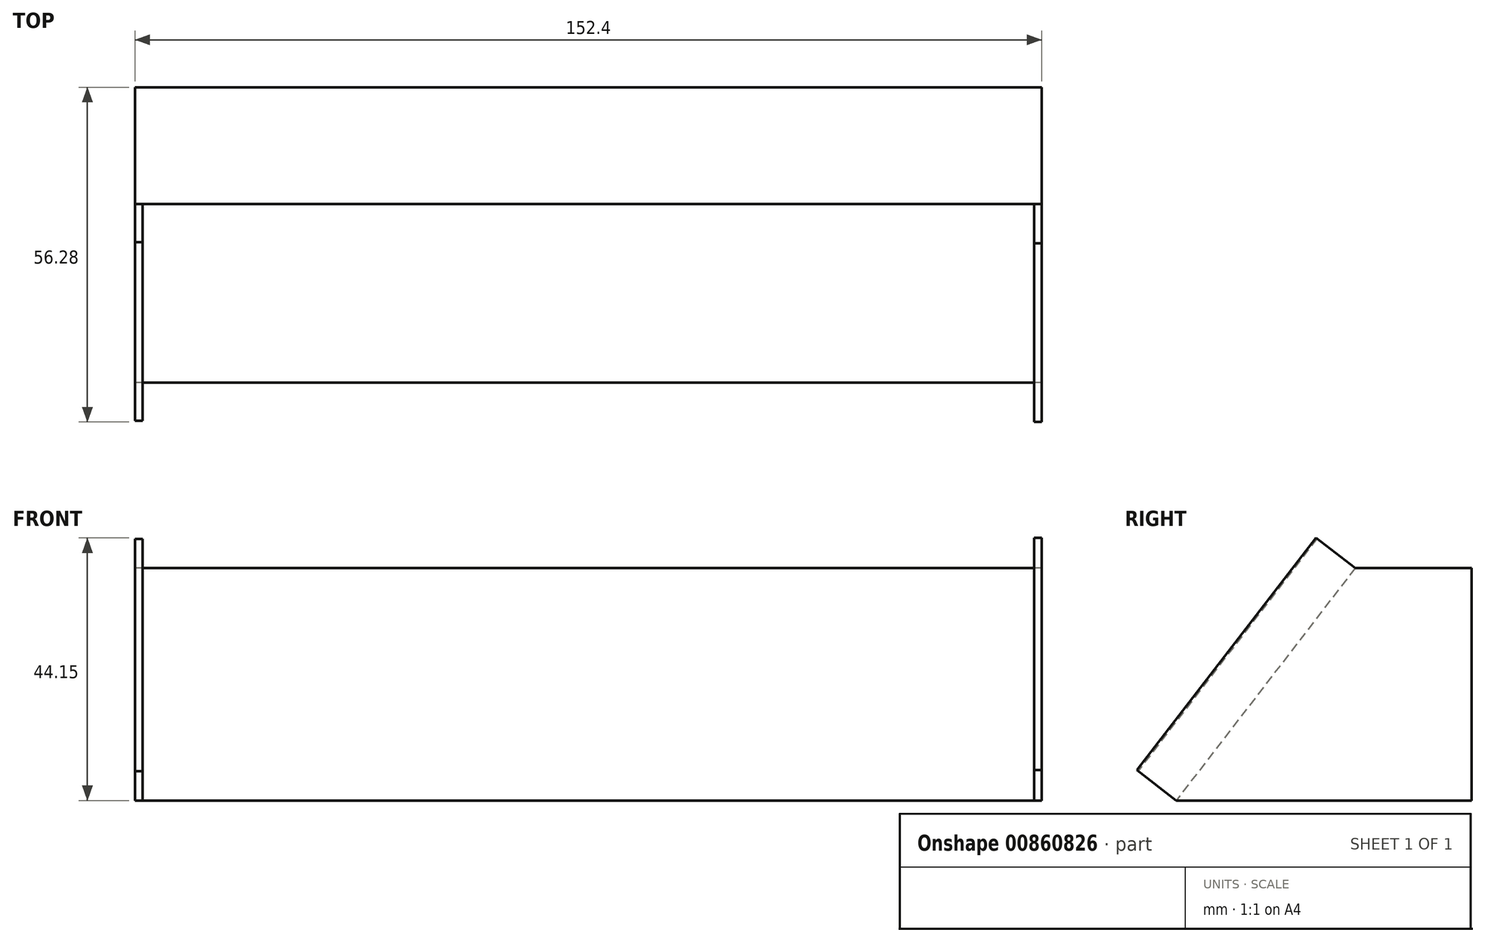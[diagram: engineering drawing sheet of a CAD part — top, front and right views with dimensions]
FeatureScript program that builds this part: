
annotation { "Feature Type Name" : "Feature", "Feature Type Description" : "" }
export const myFeature = defineFeature(function(context is Context, id is Id, definition is map)
    precondition{}
    {
        {
            var Q0;
            Q0=qCreatedBy(makeId("Right.planeOp"),FACE);
            var sketch = newSketch(context, id + "F0", { "sketchPlane" : qUnion([Q0])});
            skLineSegment(sketch, "E0", {"start": v(-3.9, 0) * mm, "end": v(26.18, 0) * mm});
            skLineSegment(sketch, "E1", {"start": v(26.18, 39.07) * mm, "end": v(-3.9, 0) * mm});
            skPoint(sketch, "E2.orphan", {"position": v(-22.96, 0) * mm});
            skLineSegment(sketch, "E3.bottom", {"start": v(26.18, 39.07) * mm, "end": v(45.78, 39.07) * mm});
            skLineSegment(sketch, "E3.top", {"start": v(26.18, 0) * mm, "end": v(45.78, 0) * mm});
            skLineSegment(sketch, "E3.right", {"start": v(45.78, 39.07) * mm, "end": v(45.78, 0) * mm});
            skSolve(sketch);
        }
        {
            var Q0;
            Q0 = qSketchRegion(id + "F0", true);
            extrude(context, id + "F1", {"entities" : qUnion([Q0]), "endBound" : BoundingType.SYMMETRIC, "depth" : 152.4 * mm, "offsetDistance" : 25.4 * mm});
        }
        {
            var Q0;
            Q0=makeQuery(id+"F1.opExtrude","CAP_FACE",FACE,{"disambiguationData":[OSD([sQuery(id+"F0.wireOp",EDGE,"E0"),sQuery(id+"F0.wireOp",EDGE,"E1"),sQuery(id+"F0.wireOp",EDGE,"E3.bottom"),sQuery(id+"F0.wireOp",EDGE,"E3.top"),sQuery(id+"F0.wireOp",EDGE,"E3.right")])],"isStart":false});
            var sketch = newSketch(context, id + "F2", { "sketchPlane" : qUnion([Q0])});
            skLineSegment(sketch, "E4", {"start": v(-3.9, 0) * mm, "end": v(-10.5, 5.09) * mm});
            skLineSegment(sketch, "E5", {"start": v(-10.5, 5.09) * mm, "end": v(19.57, 44.15) * mm});
            skLineSegment(sketch, "E6", {"start": v(19.57, 44.15) * mm, "end": v(26.18, 39.07) * mm});
            skLineSegment(sketch, "E7", {"start": v(26.18, 39.07) * mm, "end": v(-3.9, 0) * mm});
            skSolve(sketch);
        }
        {
            var Q0;
            Q0 = qSketchRegion(id + "F2", true);
            extrude(context, id + "F3", {"entities" : qUnion([Q0]), "operationType" : NewBodyOperationType.ADD, "oppositeDirection" : true, "depth" : 1.27 * mm, "offsetDistance" : 25.4 * mm});
        }
        {
            var Q0;
            Q0=makeQuery(id+"F1.opExtrude","CAP_FACE",FACE,{"disambiguationData":[OSD([sQuery(id+"F0.wireOp",EDGE,"E0"),sQuery(id+"F0.wireOp",EDGE,"E1"),sQuery(id+"F0.wireOp",EDGE,"E3.bottom"),sQuery(id+"F0.wireOp",EDGE,"E3.top"),sQuery(id+"F0.wireOp",EDGE,"E3.right")])],"isStart":true});
            var sketch = newSketch(context, id + "F4", { "sketchPlane" : qUnion([Q0])});
            skLineSegment(sketch, "E8", {"start": v(-26.18, 39.07) * mm, "end": v(-19.75, 44.01) * mm});
            skLineSegment(sketch, "E9", {"start": v(-19.75, 44.01) * mm, "end": v(10.32, 4.95) * mm});
            skLineSegment(sketch, "E10", {"start": v(10.32, 4.95) * mm, "end": v(3.9, 0) * mm});
            skLineSegment(sketch, "E11", {"start": v(-26.18, 39.07) * mm, "end": v(3.9, 0) * mm});
            skSolve(sketch);
        }
        {
            var Q0;
            Q0 = qSketchRegion(id + "F4", true);
            extrude(context, id + "F5", {"entities" : qUnion([Q0]), "operationType" : NewBodyOperationType.ADD, "oppositeDirection" : true, "depth" : 1.27 * mm, "offsetDistance" : 25.4 * mm});
        }
    });
